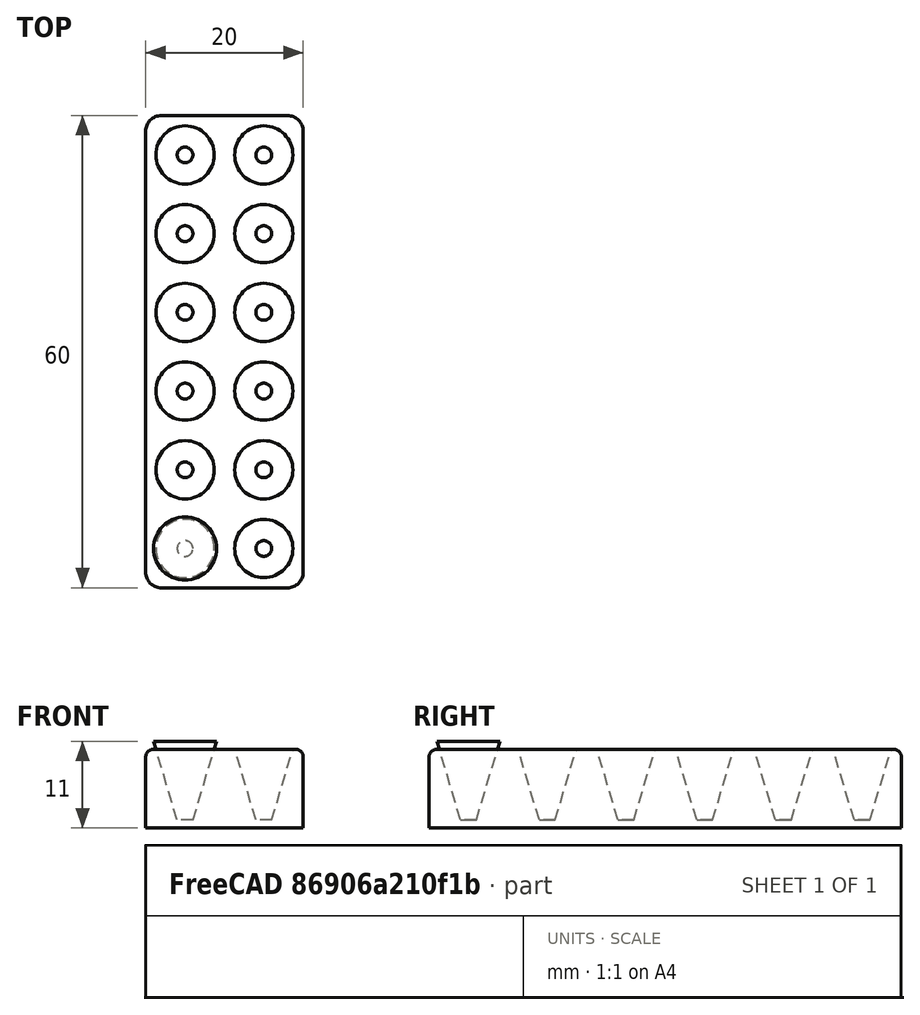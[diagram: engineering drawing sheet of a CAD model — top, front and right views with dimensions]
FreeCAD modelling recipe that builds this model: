
FCSTD DOCUMENT  (FreeCAD 0.20R29603 (Git))
Label: Ielkadi_repte2
License: All rights reserved
LicenseURL: http://en.wikipedia.org/wiki/All_rights_reserved
objects: Part::Fillet×2, Part::Box×1, Part::Cone×1, Part::FeaturePython×1, Part::Cut×1
note: 5 computed .brp shape members not serialized (recipe doc carries the construction recipe); baked Part::Feature solids carry a one-line shape summary decoded from their .brp

FEATURE [Part::Box] Box  label="Cub"
  AttacherType = Attacher::AttachEngine3D
  Height = 10
  Length = 20
  Width = 60
FEATURE [Part::Cone] Cone  label="Con"
  Angle = 360
  AttacherType = Attacher::AttachEngine3D
  Height = 10
  Placement = pos=(5,5,1) rot=(0,0,1;0rad)
  Radius1 = 1
  Radius2 = 4
FEATURE [Part::FeaturePython] Array  label="Array de cubs"  # Draft array (typed FeaturePython)
  AlwaysSyncPlacement = false
  Angle = 360
  ArrayType = 0
  Axis = (0,0,1)
  Base = -> Cone
  Center = (0,0,0)
  Count = 12
  ExpandArray = false
  Fuse = false
  IntervalAxis = (0,0,0)
  IntervalX = (10,0,0)
  IntervalY = (0,10,0)
  IntervalZ = (0,0,100)
  NumberCircles = 3
  NumberPolar = 5
  NumberX = 2
  NumberY = 6
  NumberZ = 1
  PlacementList = 12 placements: [(5,5,1),(5,15,1),(5,25,1),(5,35,1),(5,45,1),(5,55,1),(15,5,1),(15,15,1),(15,25,1),(15,35,1),(15,45,1),(15,55,1)]
  RadialDistance = 50
  ScaleList = (12) [(1,1,1),(1,1,1),(1,1,1),(1,1,1),(1,1,1),(1,1,1),(1,1,1),(1,1,1),(1,1,1),(1,1,1),(1,1,1),(1,1,1)]
  Symmetry = 1
  TangentialDistance = 25
FEATURE [Part::Fillet] Fillet  label="Cub final"
  Base = -> Box
  Edges = 4 edges r=2: [Edge1,Edge3,Edge5,Edge7]
FEATURE [Part::Cut] Cut  label="Peça final"
  Base = -> Fillet
  Tool = -> Array
FEATURE [Part::Fillet] Fillet001
  Base = -> Cut
  Edges = 8 edges r=1: [Edge1,Edge5,Edge6,Edge7,Edge8,Edge9,Edge10,Edge11]
